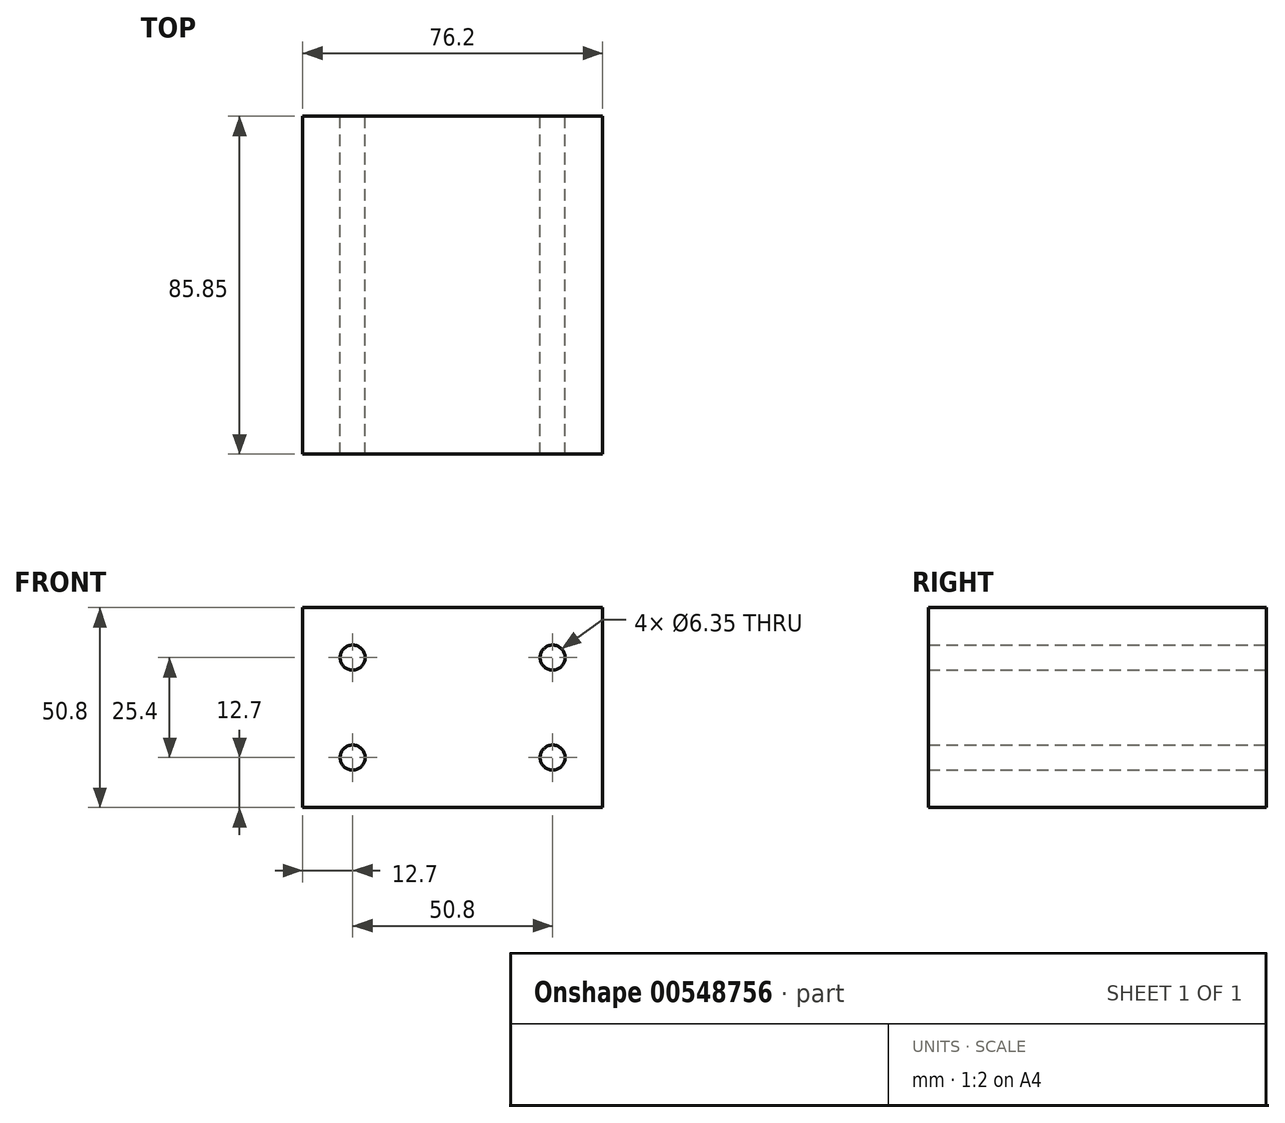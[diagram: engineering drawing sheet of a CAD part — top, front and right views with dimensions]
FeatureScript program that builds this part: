
annotation { "Feature Type Name" : "Feature", "Feature Type Description" : "" }
export const myFeature = defineFeature(function(context is Context, id is Id, definition is map)
    precondition{}
    {
        {
            var Q0;
            Q0=qCreatedBy(makeId("Front.planeOp"),FACE);
            var sketch = newSketch(context, id + "F0", { "sketchPlane" : qUnion([Q0])});
            skLineSegment(sketch, "E0.bottom", {"start": v(-38.1, 25.4) * mm, "end": v(38.1, 25.4) * mm});
            skLineSegment(sketch, "E0.top", {"start": v(-38.1, -25.4) * mm, "end": v(38.1, -25.4) * mm});
            skLineSegment(sketch, "E0.left", {"start": v(-38.1, 25.4) * mm, "end": v(-38.1, -25.4) * mm});
            skLineSegment(sketch, "E0.right", {"start": v(38.1, 25.4) * mm, "end": v(38.1, -25.4) * mm});
            skPoint(sketch, "E0.middle", {"position": v(0, 0) * mm});
            skCircle(sketch, "E1", {"center": v(-25.4, 12.7) * mm, "radius": 3.18 * mm});
            skCircle(sketch, "E2", {"center": v(25.4, 12.7) * mm, "radius": 3.18 * mm});
            skCircle(sketch, "E3", {"center": v(-25.4, -12.7) * mm, "radius": 3.18 * mm});
            skCircle(sketch, "E4", {"center": v(25.4, -12.7) * mm, "radius": 3.18 * mm});
            skSolve(sketch);
        }
        {
            var Q0;
            Q0=makeQuery(id+"F0.imprint","IMPRINT",FACE,{"disambiguationData":[TD([[makeQuery(id+"F0.imprint","IMPRINT",EDGE,{"derivedFrom":sQuery(id+"F0.wireOp",EDGE,"E0.bottom")}),-1.0]])]});
            extrude(context, id + "F1", {"entities" : qUnion([Q0]), "depth" : 85.85 * mm, "offsetDistance" : 25.4 * mm});
        }
    });
